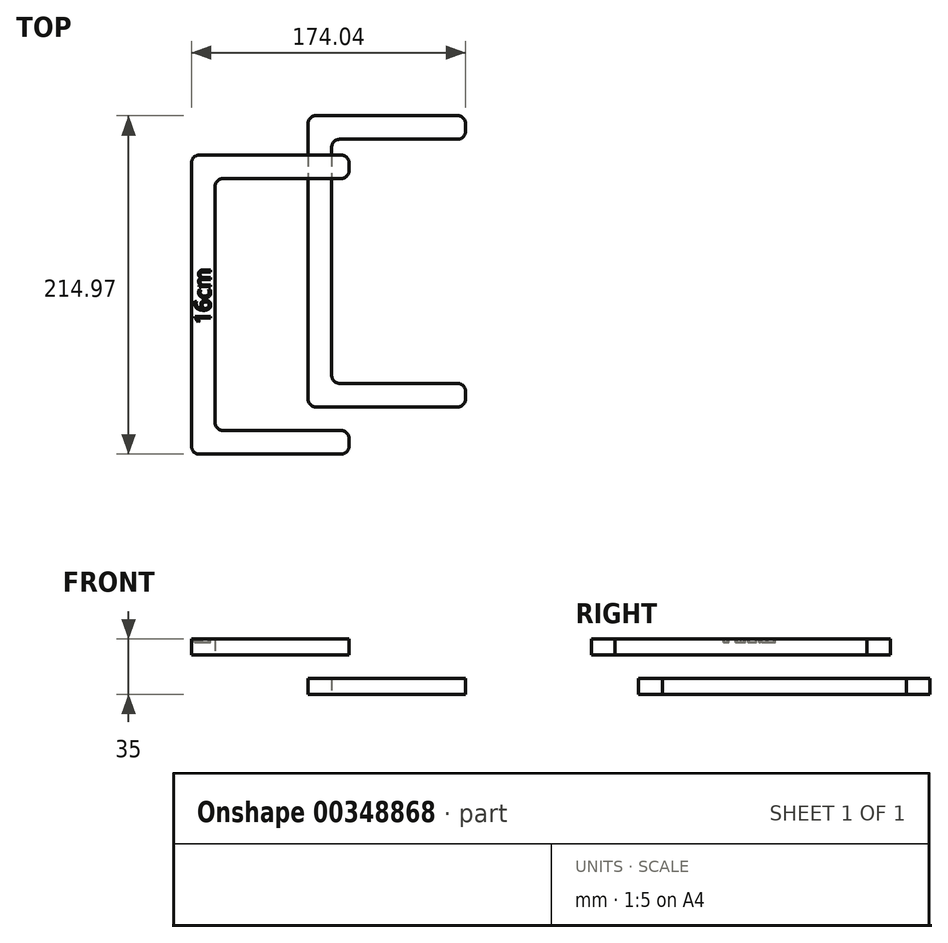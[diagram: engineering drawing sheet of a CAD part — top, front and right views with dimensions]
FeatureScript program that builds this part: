
annotation { "Feature Type Name" : "Feature", "Feature Type Description" : "" }
export const myFeature = defineFeature(function(context is Context, id is Id, definition is map)
    precondition{}
    {
        {
            var Q0;
            Q0=qCreatedBy(makeId("Top.planeOp"),FACE);
            cPlane(context, id + "F0", {"entities" : qUnion([Q0]), "cplaneType" : CPlaneType.OFFSET, "offset" : 25 * mm, "width" : 150 * mm, "height" : 150 * mm});
        }
        {
            var Q0;
            Q0=qCreatedBy(makeId("Top.planeOp"),FACE);
            var sketch = newSketch(context, id + "F1", { "sketchPlane" : qUnion([Q0])});
            skLineSegment(sketch, "E0.bottom", {"start": v(-26.29, 74.17) * mm, "end": v(-11.29, 74.17) * mm});
            skLineSegment(sketch, "E0.top", {"start": v(-26.29, -80.83) * mm, "end": v(-11.29, -80.83) * mm});
            skLineSegment(sketch, "E0.left", {"start": v(-26.29, 74.17) * mm, "end": v(-26.29, -80.83) * mm});
            skLineSegment(sketch, "E0.right", {"start": v(-11.29, 74.17) * mm, "end": v(-11.29, -80.83) * mm});
            skLineSegment(sketch, "E1.bottom", {"start": v(-26.29, 74.17) * mm, "end": v(73.71, 74.17) * mm});
            skLineSegment(sketch, "E1.top", {"start": v(-26.29, 89.17) * mm, "end": v(73.71, 89.17) * mm});
            skLineSegment(sketch, "E1.left", {"start": v(-26.29, 74.17) * mm, "end": v(-26.29, 89.17) * mm});
            skLineSegment(sketch, "E1.right", {"start": v(73.71, 74.17) * mm, "end": v(73.71, 89.17) * mm});
            skLineSegment(sketch, "E2.bottom", {"start": v(-26.29, -80.83) * mm, "end": v(73.71, -80.83) * mm});
            skLineSegment(sketch, "E2.top", {"start": v(-26.29, -95.83) * mm, "end": v(73.71, -95.83) * mm});
            skLineSegment(sketch, "E2.left", {"start": v(-26.29, -80.83) * mm, "end": v(-26.29, -95.83) * mm});
            skLineSegment(sketch, "E2.right", {"start": v(73.71, -80.83) * mm, "end": v(73.71, -95.83) * mm});
            skSolve(sketch);
        }
        {
            var Q0;
            {var subQ0=sQuery(id+"F1.wireOp",EDGE,"E0.left");Q0=makeQuery(id+"F1.imprint","IMPRINT",FACE,{"disambiguationData":[TD([[makeQuery(id+"F1.imprint","IMPRINT",EDGE,{"derivedFrom":subQ0}),1.0]])]});}
            var Q1;
            Q1=makeQuery(id+"F1.imprint","IMPRINT",FACE,{"disambiguationData":[TD([[makeQuery(id+"F1.imprint","IMPRINT",EDGE,{"derivedFrom":sQuery(id+"F1.wireOp",EDGE,"E2.top")}),1.0]])]});
            var Q2;
            Q2=makeQuery(id+"F1.imprint","IMPRINT",FACE,{"disambiguationData":[TD([[makeQuery(id+"F1.imprint","IMPRINT",EDGE,{"derivedFrom":sQuery(id+"F1.wireOp",EDGE,"E1.top")}),-1.0]])]});
            extrude(context, id + "F2", {"entities" : qUnion([Q0, Q1, Q2]), "depth" : 10 * mm});
        }
        {
            var Q0;
            Q0=makeQuery(id+"F2.opExtrude","SWEPT_EDGE",EDGE,{"disambiguationData":[OSD([sQuery(id+"F1.wireOp",EDGE,"E1.top"),sQuery(id+"F1.wireOp",EDGE,"E1.left")])]});
            var Q1;
            Q1=makeQuery(id+"F2.opExtrude","SWEPT_EDGE",EDGE,{"disambiguationData":[OSD([sQuery(id+"F1.wireOp",EDGE,"E2.top"),sQuery(id+"F1.wireOp",EDGE,"E2.left")])]});
            var Q2;
            Q2=makeQuery(id+"F2.opExtrude","SWEPT_EDGE",EDGE,{"disambiguationData":[OSD([sQuery(id+"F1.wireOp",EDGE,"E0.right"),sQuery(id+"F1.wireOp",EDGE,"E2.bottom")])]});
            var Q3;
            Q3=makeQuery(id+"F2.opExtrude","SWEPT_EDGE",EDGE,{"disambiguationData":[OSD([sQuery(id+"F1.wireOp",EDGE,"E0.right"),sQuery(id+"F1.wireOp",EDGE,"E1.bottom")])]});
            var Q4;
            Q4=makeQuery(id+"F2.opExtrude","SWEPT_EDGE",EDGE,{"disambiguationData":[OSD([sQuery(id+"F1.wireOp",EDGE,"E1.bottom"),sQuery(id+"F1.wireOp",EDGE,"E1.right")])]});
            var Q5;
            Q5=makeQuery(id+"F2.opExtrude","SWEPT_EDGE",EDGE,{"disambiguationData":[OSD([sQuery(id+"F1.wireOp",EDGE,"E2.bottom"),sQuery(id+"F1.wireOp",EDGE,"E2.right")])]});
            var Q6;
            Q6=makeQuery(id+"F2.opExtrude","SWEPT_EDGE",EDGE,{"disambiguationData":[OSD([sQuery(id+"F1.wireOp",EDGE,"E2.top"),sQuery(id+"F1.wireOp",EDGE,"E2.right")])]});
            var Q7;
            Q7=makeQuery(id+"F2.opExtrude","SWEPT_EDGE",EDGE,{"disambiguationData":[OSD([sQuery(id+"F1.wireOp",EDGE,"E1.top"),sQuery(id+"F1.wireOp",EDGE,"E1.right")])]});
            fillet(context, id + "F3", {"entities" : qUnion([Q0, Q1, Q2, Q3, Q4, Q5, Q6, Q7]), "radius" : 5 * mm, "tangentPropagation" : true, "allowEdgeOverflow" : false});
        }
        {
            var Q0;
            Q0=qCreatedBy(id+"F0.planeOp",FACE);
            var sketch = newSketch(context, id + "F4", { "sketchPlane" : qUnion([Q0])});
            skLineSegment(sketch, "E3.bottom", {"start": v(-100.33, 49.2) * mm, "end": v(-85.33, 49.2) * mm});
            skLineSegment(sketch, "E3.top", {"start": v(-100.33, -110.8) * mm, "end": v(-85.33, -110.8) * mm});
            skLineSegment(sketch, "E3.left", {"start": v(-100.33, 49.2) * mm, "end": v(-100.33, -110.8) * mm});
            skLineSegment(sketch, "E3.right", {"start": v(-85.33, 49.2) * mm, "end": v(-85.33, -110.8) * mm});
            skLineSegment(sketch, "E4.bottom", {"start": v(-100.33, 49.2) * mm, "end": v(-0.33, 49.2) * mm});
            skLineSegment(sketch, "E4.top", {"start": v(-100.33, 64.2) * mm, "end": v(-0.33, 64.2) * mm});
            skLineSegment(sketch, "E4.left", {"start": v(-100.33, 49.2) * mm, "end": v(-100.33, 64.2) * mm});
            skLineSegment(sketch, "E4.right", {"start": v(-0.33, 49.2) * mm, "end": v(-0.33, 64.2) * mm});
            skLineSegment(sketch, "E5.bottom", {"start": v(-100.33, -110.8) * mm, "end": v(-0.33, -110.8) * mm});
            skLineSegment(sketch, "E5.top", {"start": v(-100.33, -125.8) * mm, "end": v(-0.33, -125.8) * mm});
            skLineSegment(sketch, "E5.left", {"start": v(-100.33, -110.8) * mm, "end": v(-100.33, -125.8) * mm});
            skLineSegment(sketch, "E5.right", {"start": v(-0.33, -110.8) * mm, "end": v(-0.33, -125.8) * mm});
            skText(sketch, "E6", { "text": "16cm", "fontName": "OpenSans-Regular.ttf"});
            const initialGuessF4  = {"E6": [-0.08823, -0.04319, 0, 1, 0.01]};
            skSetInitialGuess(sketch, initialGuessF4);
            skSolve(sketch);
        }
        {
            var Q0;
            Q0=makeQuery(id+"F4.imprint","IMPRINT",FACE,{"disambiguationData":[TD([[makeQuery(id+"F4.imprint","IMPRINT",EDGE,{"derivedFrom":sQuery(id+"F4.wireOp",EDGE,"E4.top")}),-1.0]])]});
            var Q1;
            Q1=makeQuery(id+"F4.imprint","IMPRINT",FACE,{"disambiguationData":[TD([[makeQuery(id+"F4.imprint","IMPRINT",EDGE,{"derivedFrom":sQuery(id+"F4.wireOp",EDGE,"E5.top")}),1.0]])]});
            var Q2;
            {var subQ0=sQuery(id+"F4.wireOp",EDGE,"E3.left");Q2=makeQuery(id+"F4.imprint","IMPRINT",FACE,{"disambiguationData":[TD([[makeQuery(id+"F4.imprint","IMPRINT",EDGE,{"derivedFrom":subQ0}),1.0]])]});}
            var Q3;
            Q3 = qSketchRegion(id + "F4", true);
            var Q4;
            Q4=makeQuery(id+"F4.imprint","IMPRINT",FACE,{"disambiguationData":[TD([[makeQuery(id+"F4.imprint","IMPRINT",EDGE,{"derivedFrom":sQuery(id+"F4.wireOp",EDGE,"E6.sketch_text.stroke-0")}),-1.0]])]});
            var Q5;
            Q5=makeQuery(id+"F4.imprint","IMPRINT",FACE,{"disambiguationData":[TD([[makeQuery(id+"F4.imprint","IMPRINT",EDGE,{"derivedFrom":sQuery(id+"F4.wireOp",EDGE,"E6.sketch_text.stroke-24")}),1.0]])]});
            var Q6;
            Q6=makeQuery(id+"F4.imprint","IMPRINT",FACE,{"disambiguationData":[TD([[makeQuery(id+"F4.imprint","IMPRINT",EDGE,{"derivedFrom":sQuery(id+"F4.wireOp",EDGE,"E6.sketch_text.stroke-34")}),-1.0]])]});
            var Q7;
            Q7=makeQuery(id+"F4.imprint","IMPRINT",FACE,{"disambiguationData":[TD([[makeQuery(id+"F4.imprint","IMPRINT",EDGE,{"derivedFrom":sQuery(id+"F4.wireOp",EDGE,"E6.sketch_text.stroke-49")}),-1.0]])]});
            var Q8;
            Q8=makeQuery(id+"F4.imprint","IMPRINT",FACE,{"disambiguationData":[TD([[makeQuery(id+"F4.imprint","IMPRINT",EDGE,{"derivedFrom":sQuery(id+"F4.wireOp",EDGE,"E6.sketch_text.stroke-9")}),-1.0]])]});
            extrude(context, id + "F5", {"entities" : qUnion([Q0, Q1, Q2, Q3, Q4, Q5, Q6, Q7, Q8]), "depth" : 10 * mm});
        }
        {
            var Q0;
            Q0=makeQuery(id+"F5.opExtrude","CAP_FACE",FACE,{"disambiguationData":[OSD([sQuery(id+"F4.wireOp",EDGE,"E3.left"),sQuery(id+"F4.wireOp",EDGE,"E3.right"),sQuery(id+"F4.wireOp",EDGE,"E4.bottom"),sQuery(id+"F4.wireOp",EDGE,"E4.top"),sQuery(id+"F4.wireOp",EDGE,"E4.left"),sQuery(id+"F4.wireOp",EDGE,"E4.right"),sQuery(id+"F4.wireOp",EDGE,"E5.bottom"),sQuery(id+"F4.wireOp",EDGE,"E5.top"),sQuery(id+"F4.wireOp",EDGE,"E5.left"),sQuery(id+"F4.wireOp",EDGE,"E5.right")])],"isStart":false});
            var sketch = newSketch(context, id + "F6", { "sketchPlane" : qUnion([Q0])});
            skText(sketch, "E7", { "text": "16cm", "fontName": "OpenSans-Regular.ttf"});
            const initialGuessF6  = {"E7": [-0.08823, -0.04319, 0, 1, 0.01]};
            skSetInitialGuess(sketch, initialGuessF6);
            skSolve(sketch);
        }
        {
            var Q0;
            Q0 = qSketchRegion(id + "F6", true);
            extrude(context, id + "F7", {"entities" : qUnion([Q0]), "operationType" : NewBodyOperationType.REMOVE, "oppositeDirection" : true, "depth" : 2 * mm});
        }
        {
            var Q0;
            Q0=makeQuery(id+"F5.opExtrude","SWEPT_EDGE",EDGE,{"disambiguationData":[OSD([sQuery(id+"F4.wireOp",EDGE,"E4.top"),sQuery(id+"F4.wireOp",EDGE,"E4.left")])]});
            var Q1;
            Q1=makeQuery(id+"F5.opExtrude","SWEPT_EDGE",EDGE,{"disambiguationData":[OSD([sQuery(id+"F4.wireOp",EDGE,"E5.top"),sQuery(id+"F4.wireOp",EDGE,"E5.left")])]});
            var Q2;
            Q2=makeQuery(id+"F5.opExtrude","SWEPT_EDGE",EDGE,{"disambiguationData":[OSD([sQuery(id+"F4.wireOp",EDGE,"E5.top"),sQuery(id+"F4.wireOp",EDGE,"E5.right")])]});
            var Q3;
            Q3=makeQuery(id+"F5.opExtrude","SWEPT_EDGE",EDGE,{"disambiguationData":[OSD([sQuery(id+"F4.wireOp",EDGE,"E5.bottom"),sQuery(id+"F4.wireOp",EDGE,"E5.right")])]});
            var Q4;
            Q4=makeQuery(id+"F5.opExtrude","SWEPT_EDGE",EDGE,{"disambiguationData":[OSD([sQuery(id+"F4.wireOp",EDGE,"E4.bottom"),sQuery(id+"F4.wireOp",EDGE,"E4.right")])]});
            var Q5;
            Q5=makeQuery(id+"F5.opExtrude","SWEPT_EDGE",EDGE,{"disambiguationData":[OSD([sQuery(id+"F4.wireOp",EDGE,"E4.top"),sQuery(id+"F4.wireOp",EDGE,"E4.right")])]});
            var Q6;
            Q6=makeQuery(id+"F5.opExtrude","SWEPT_EDGE",EDGE,{"disambiguationData":[OSD([sQuery(id+"F4.wireOp",EDGE,"E3.right"),sQuery(id+"F4.wireOp",EDGE,"E4.bottom")])]});
            var Q7;
            Q7=makeQuery(id+"F5.opExtrude","SWEPT_EDGE",EDGE,{"disambiguationData":[OSD([sQuery(id+"F4.wireOp",EDGE,"E3.right"),sQuery(id+"F4.wireOp",EDGE,"E5.bottom")])]});
            fillet(context, id + "F8", {"entities" : qUnion([Q0, Q1, Q2, Q3, Q4, Q5, Q6, Q7]), "radius" : 5 * mm, "tangentPropagation" : true, "allowEdgeOverflow" : false});
        }
    });
